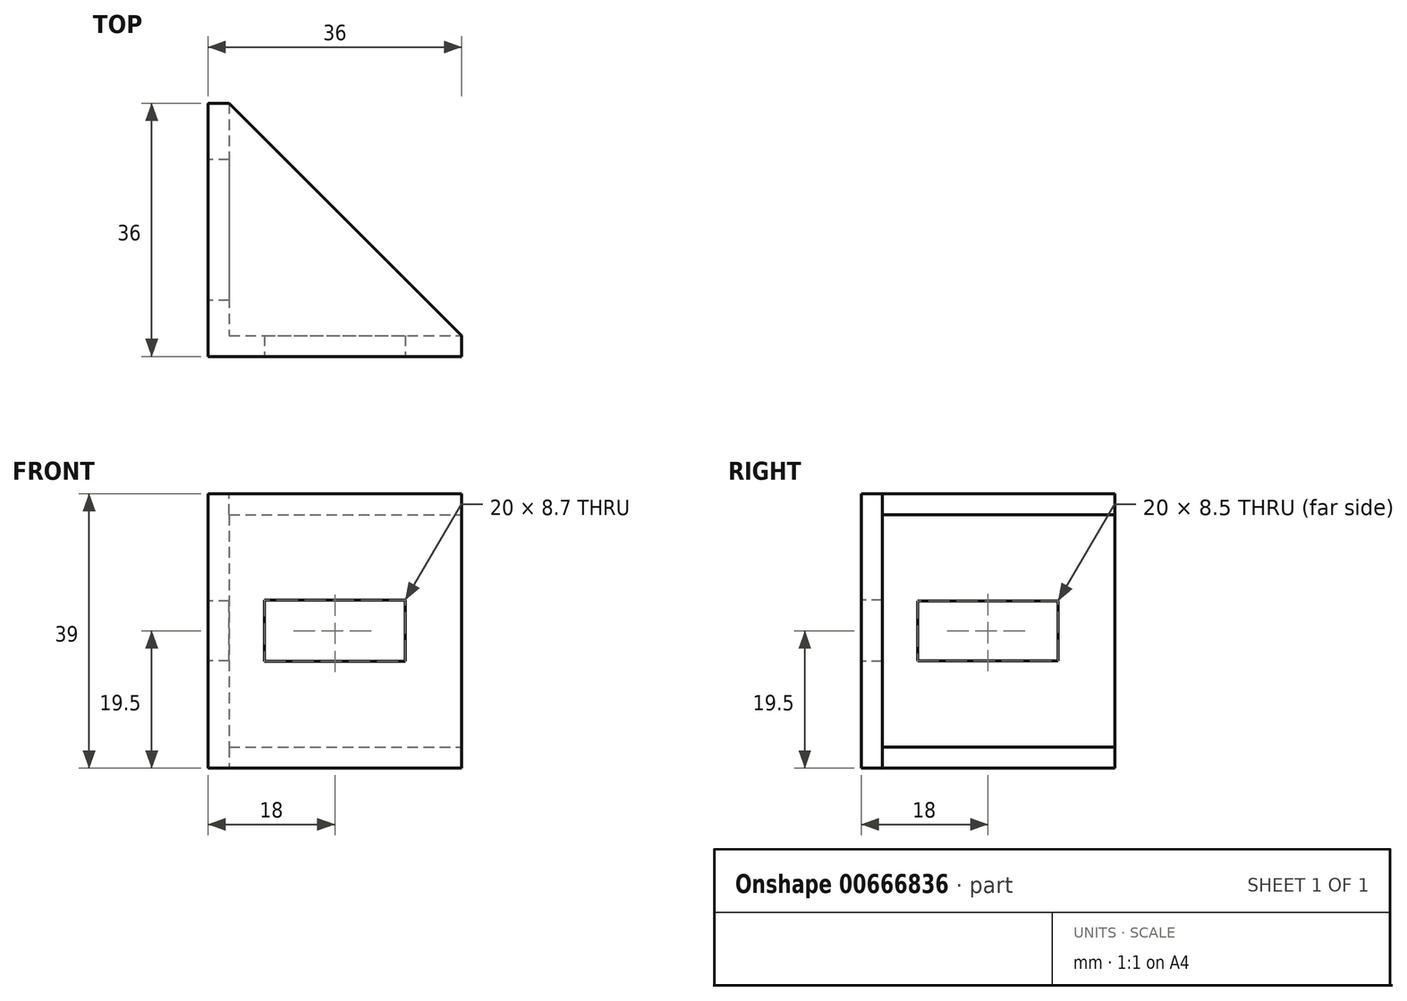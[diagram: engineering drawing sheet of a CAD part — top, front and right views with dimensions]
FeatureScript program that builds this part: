
annotation { "Feature Type Name" : "Feature", "Feature Type Description" : "" }
export const myFeature = defineFeature(function(context is Context, id is Id, definition is map)
    precondition{}
    {
        {
            var Q0;
            Q0=qCreatedBy(makeId("Top.planeOp"),FACE);
            var sketch = newSketch(context, id + "F0", { "sketchPlane" : qUnion([Q0])});
            skLineSegment(sketch, "E0", {"start": v(0, 0) * mm, "end": v(36, 0) * mm});
            skLineSegment(sketch, "E1", {"start": v(0, 0) * mm, "end": v(0, 36) * mm});
            skLineSegment(sketch, "E2", {"start": v(0, 36) * mm, "end": v(3, 36) * mm});
            skLineSegment(sketch, "E3", {"start": v(36, 0) * mm, "end": v(36, 3) * mm});
            skLineSegment(sketch, "E4", {"start": v(36, 3) * mm, "end": v(3, 36) * mm});
            skSolve(sketch);
        }
        {
            var Q0;
            Q0=makeQuery(id+"F0.imprint","IMPRINT",FACE,{"disambiguationData":[TD([[makeQuery(id+"F0.imprint","IMPRINT",EDGE,{"derivedFrom":sQuery(id+"F0.wireOp",EDGE,"E0")}),1.0]])]});
            extrude(context, id + "F1", {"entities" : qUnion([Q0]), "depth" : 3 * mm, "offsetDistance" : 25 * mm});
        }
        {
            var Q0;
            Q0=makeQuery(id+"F1.opExtrude","CAP_FACE",FACE,{"disambiguationData":[OSD([sQuery(id+"F0.wireOp",EDGE,"E0"),sQuery(id+"F0.wireOp",EDGE,"E1"),sQuery(id+"F0.wireOp",EDGE,"E2"),sQuery(id+"F0.wireOp",EDGE,"E3"),sQuery(id+"F0.wireOp",EDGE,"E4")])],"isStart":false});
            var sketch = newSketch(context, id + "F2", { "sketchPlane" : qUnion([Q0])});
            skLineSegment(sketch, "E5", {"start": v(3, 36) * mm, "end": v(3, 3) * mm});
            skLineSegment(sketch, "E6", {"start": v(3, 3) * mm, "end": v(36, 3) * mm});
            skSolve(sketch);
        }
        {
            var Q0;
            Q0=makeQuery(id+"F2.imprint","IMPRINT",FACE,{"disambiguationData":[TD([[makeQuery(id+"F2.imprint","IMPRINT",EDGE,{"derivedFrom":sQuery(id+"F2.wireOp",EDGE,"E5")}),-1.0]])]});
            extrude(context, id + "F3", {"entities" : qUnion([Q0]), "operationType" : NewBodyOperationType.ADD, "depth" : 16.5 * mm, "offsetDistance" : 25 * mm});
        }
        {
            var Q0;
            Q0=makeQuery(id+"F1.opExtrude","SWEPT_BODY",BODY,{"disambiguationData":[OSD([sQuery(id+"F0.wireOp",EDGE,"E0"),sQuery(id+"F0.wireOp",EDGE,"E1"),sQuery(id+"F0.wireOp",EDGE,"E2"),sQuery(id+"F0.wireOp",EDGE,"E3"),sQuery(id+"F0.wireOp",EDGE,"E4")])]});
            var Q1;
            Q1=makeQuery(id+"F3.opExtrude","CAP_FACE",FACE,{"disambiguationData":[OSD([sQuery(id+"F0.wireOp",EDGE,"E0"),sQuery(id+"F0.wireOp",EDGE,"E1"),sQuery(id+"F0.wireOp",EDGE,"E2"),sQuery(id+"F0.wireOp",EDGE,"E3"),sQuery(id+"F2.wireOp",EDGE,"E5"),sQuery(id+"F2.wireOp",EDGE,"E6")])],"isStart":false});
            mirror(context, id + "F4", {"operationType" : NewBodyOperationType.ADD, "entities" : qUnion([Q0]), "mirrorPlane" : qUnion([Q1])});
        }
        {
            var Q0;
            {var subQ0=sQuery(id+"F0.wireOp",EDGE,"E0");var subQ1=makeQuery(id+"F3.boolean.opBoolean","MERGE",FACE,{"derivedFrom":[makeQuery(id+"F1.opExtrude","SWEPT_FACE",FACE,{"disambiguationData":[OSD([subQ0])]}),makeQuery(id+"F3.opExtrude","SWEPT_FACE",FACE,{"disambiguationData":[OSD([subQ0])]})]});Q0=makeQuery(id+"F4.boolean.opBoolean","MERGE",FACE,{"derivedFrom":[subQ1,makeQuery(id+"F4.opPattern","COPY",FACE,{"derivedFrom":subQ1,"instanceName":"1"})]});}
            var sketch = newSketch(context, id + "F5", { "sketchPlane" : qUnion([Q0])});
            skLineSegment(sketch, "E7", {"start": v(18, 0) * mm, "end": v(18, 39) * mm, "construction": true});
            skLineSegment(sketch, "E8.bottom", {"start": v(28, 23.85) * mm, "end": v(8, 23.85) * mm});
            skLineSegment(sketch, "E8.top", {"start": v(28, 15.15) * mm, "end": v(8, 15.15) * mm});
            skLineSegment(sketch, "E8.left", {"start": v(28, 23.85) * mm, "end": v(28, 15.15) * mm});
            skLineSegment(sketch, "E8.right", {"start": v(8, 23.85) * mm, "end": v(8, 15.15) * mm});
            skPoint(sketch, "E8.middle", {"position": v(18, 19.5) * mm});
            skSolve(sketch);
        }
        {
            var Q0;
            Q0 = qSketchRegion(id + "F5", true);
            extrude(context, id + "F6", {"entities" : qUnion([Q0]), "operationType" : NewBodyOperationType.REMOVE, "oppositeDirection" : true, "depth" : 25 * mm, "offsetDistance" : 25 * mm});
        }
        {
            var Q0;
            {var subQ0=sQuery(id+"F0.wireOp",EDGE,"E1");var subQ1=makeQuery(id+"F3.boolean.opBoolean","MERGE",FACE,{"derivedFrom":[makeQuery(id+"F1.opExtrude","SWEPT_FACE",FACE,{"disambiguationData":[OSD([subQ0])]}),makeQuery(id+"F3.opExtrude","SWEPT_FACE",FACE,{"disambiguationData":[OSD([subQ0])]})]});Q0=makeQuery(id+"F4.boolean.opBoolean","MERGE",FACE,{"derivedFrom":[subQ1,makeQuery(id+"F4.opPattern","COPY",FACE,{"derivedFrom":subQ1,"instanceName":"1"})]});}
            var sketch = newSketch(context, id + "F7", { "sketchPlane" : qUnion([Q0])});
            skLineSegment(sketch, "E9", {"start": v(-18, 0) * mm, "end": v(-18, 39) * mm, "construction": true});
            skLineSegment(sketch, "E10.bottom", {"start": v(-8, 23.75) * mm, "end": v(-28, 23.75) * mm});
            skLineSegment(sketch, "E10.top", {"start": v(-8, 15.25) * mm, "end": v(-28, 15.25) * mm});
            skLineSegment(sketch, "E10.left", {"start": v(-8, 23.75) * mm, "end": v(-8, 15.25) * mm});
            skLineSegment(sketch, "E10.right", {"start": v(-28, 23.75) * mm, "end": v(-28, 15.25) * mm});
            skPoint(sketch, "E10.middle", {"position": v(-18, 19.5) * mm});
            skSolve(sketch);
        }
        {
            var Q0;
            Q0 = qSketchRegion(id + "F7", true);
            extrude(context, id + "F8", {"entities" : qUnion([Q0]), "operationType" : NewBodyOperationType.REMOVE, "oppositeDirection" : true, "depth" : 25 * mm, "offsetDistance" : 25 * mm});
        }
    });
